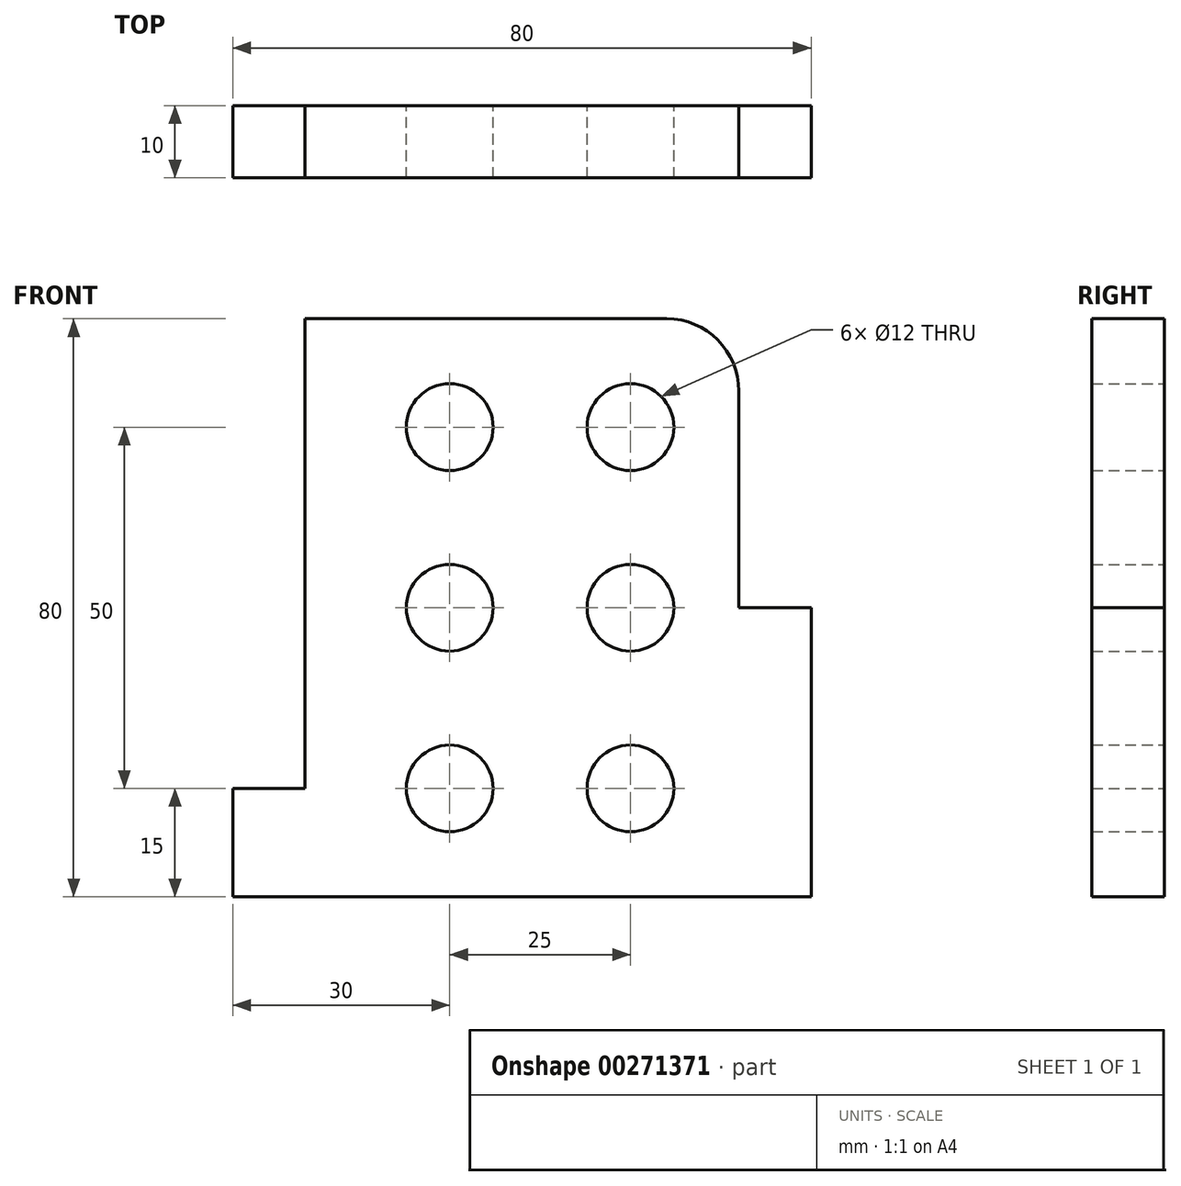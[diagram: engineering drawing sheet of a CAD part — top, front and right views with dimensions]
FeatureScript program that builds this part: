
annotation { "Feature Type Name" : "Feature", "Feature Type Description" : "" }
export const myFeature = defineFeature(function(context is Context, id is Id, definition is map)
    precondition{}
    {
        {
            var Q0;
            Q0=qCreatedBy(makeId("Front.planeOp"),FACE);
            var sketch = newSketch(context, id + "F0", { "sketchPlane" : qUnion([Q0])});
            skLineSegment(sketch, "E0", {"start": v(0, 0) * mm, "end": v(80, 0) * mm});
            skLineSegment(sketch, "E1", {"start": v(80, 0) * mm, "end": v(80, 40) * mm});
            skLineSegment(sketch, "E2", {"start": v(80, 40) * mm, "end": v(70, 40) * mm});
            skLineSegment(sketch, "E3", {"start": v(70, 40) * mm, "end": v(70, 70) * mm});
            skLineSegment(sketch, "E4", {"start": v(0, 0) * mm, "end": v(0, 15) * mm});
            skLineSegment(sketch, "E5", {"start": v(0, 15) * mm, "end": v(10, 15) * mm});
            skLineSegment(sketch, "E6", {"start": v(10, 15) * mm, "end": v(10, 80) * mm});
            skLineSegment(sketch, "E7", {"start": v(10, 80) * mm, "end": v(60, 80) * mm});
            skPoint(sketch, "E8.visualSharp", {"position": v(70, 80) * mm});
            skArc(sketch, "E8.filletArc", {"start": v(70, 70) * mm, "mid": v(67.07, 77.07) * mm, "end": v(60, 80) * mm});
            skCircle(sketch, "E9", {"center": v(30, 15) * mm, "radius": 6 * mm});
            skCircle(sketch, "E10", {"center": v(30, 40) * mm, "radius": 6 * mm});
            skCircle(sketch, "E11", {"center": v(30, 65) * mm, "radius": 6 * mm});
            skCircle(sketch, "E12", {"center": v(55, 65) * mm, "radius": 6 * mm});
            skCircle(sketch, "E13", {"center": v(55, 40) * mm, "radius": 6 * mm});
            skCircle(sketch, "E14", {"center": v(55, 15) * mm, "radius": 6 * mm});
            skSolve(sketch);
        }
        {
            var Q0;
            Q0=makeQuery(id+"F0.imprint","IMPRINT",FACE,{"disambiguationData":[TD([[makeQuery(id+"F0.imprint","IMPRINT",EDGE,{"derivedFrom":sQuery(id+"F0.wireOp",EDGE,"E0")}),1.0]])]});
            extrude(context, id + "F1", {"entities" : qUnion([Q0]), "depth" : 10 * mm});
        }
    });
